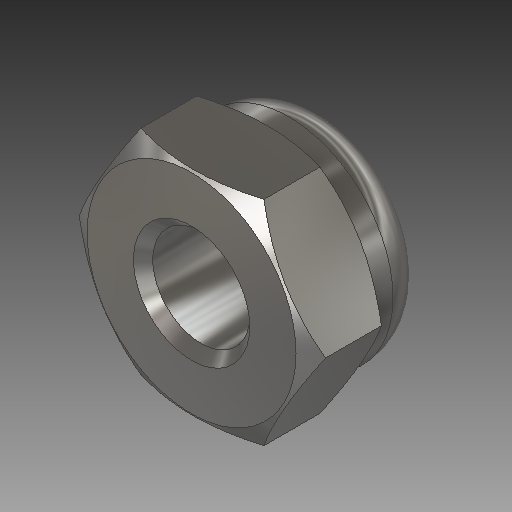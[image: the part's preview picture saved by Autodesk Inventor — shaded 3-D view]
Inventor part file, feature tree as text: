
AUTODESK INVENTOR PART (.ipt)
format: ipt  version: 2019.3 (Build 233278000, 278)  size: 234,496 bytes
history: native  units: mm
features: sketch x4, extrude x3, fillet x2, other x1, revolve x1, chamfer x1
ambient origin geometry x8: Origin, YZ Plane, XZ Plane, XY Plane, X Axis, Y Axis, Z Axis, Center Point
bodies: Body1 (feature_tree)
feature tree (12):
  other  "Твердое тело1"
  extrude  "Выдавливание1"  Depth=4.0mm TaperAngle=0.0deg
  revolve  "Вращение1"
  extrude  "Выдавливание2"  TaperAngle=60.0deg  [1 undecoded]
  fillet  "Сопряжение1"  Radius=1.0mm
  chamfer  "Фаска2"  Distance=3.5mm
  extrude  "Extrusion4"  TaperAngle=90.0deg  [1 undecoded]
  fillet  "Fillet3"  Radius=3.0mm
  sketch  "Эскиз1"
  sketch  "Эскиз2"
  sketch  "Эскиз3"
  sketch  "Sketch5"  dims[d0=5.0mm d2=4.0mm d3=0.0mm d4=60.0deg d5=1.0mm d6=3.5mm d7=90.0deg d8=3.0mm d9=0.0mm d10=2.0mm d18=0.5mm d19=2.0mm d20=45.0deg d21=3.0mm d22=0.2mm d23=0.0mm d24=0.2mm]
note: 2 required parameter values undecoded (feature->parameter linkage not recoverable at this tier; creation-order binding heuristic only, values carry confidence <= 0.55)
